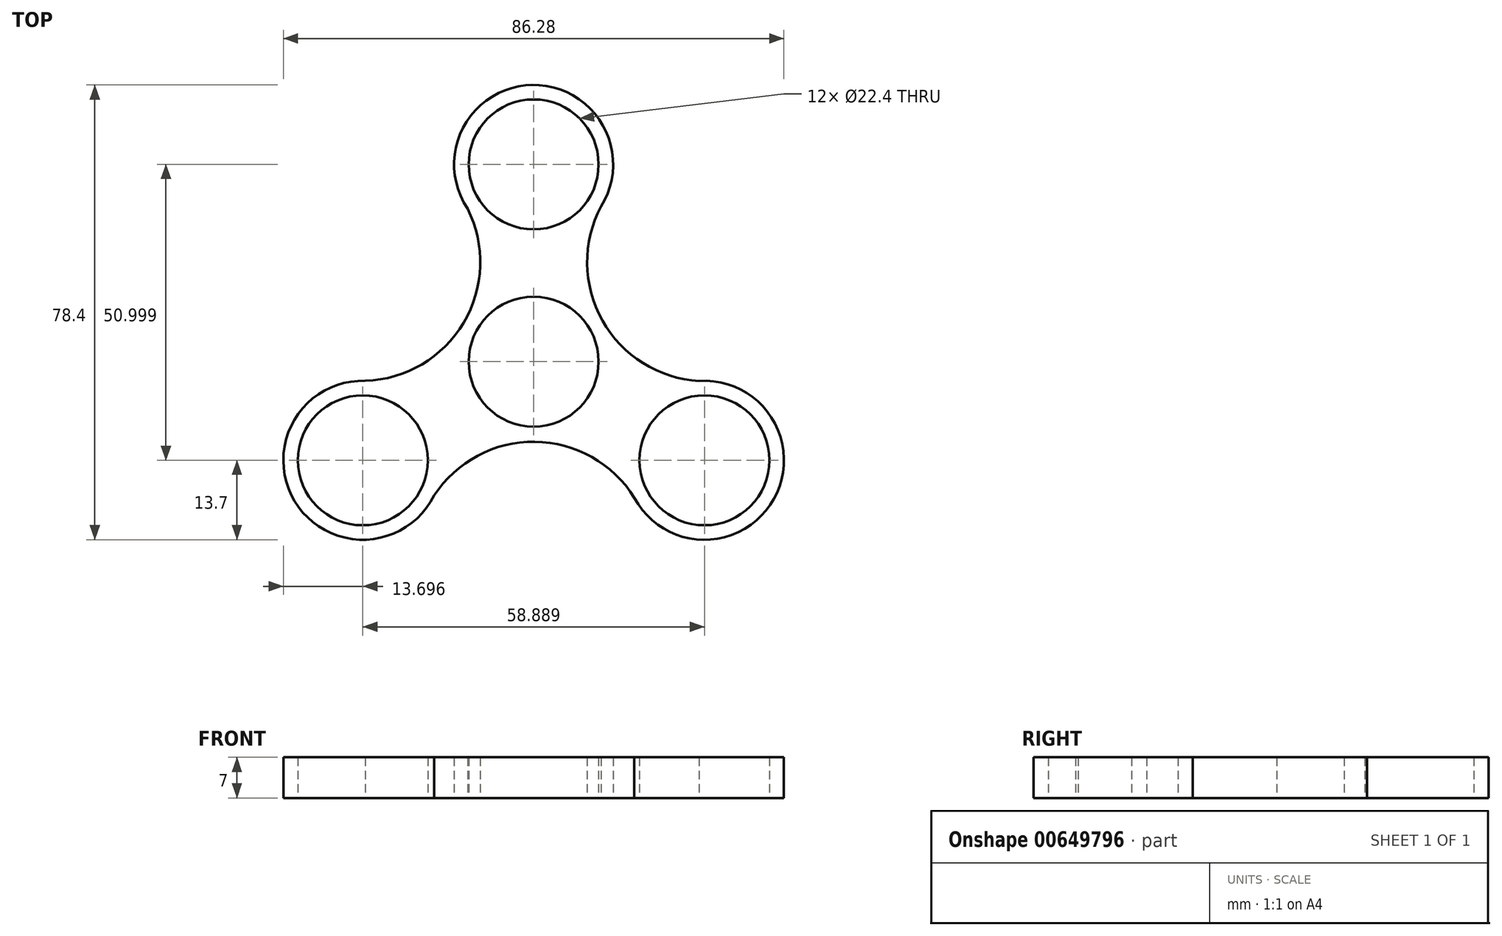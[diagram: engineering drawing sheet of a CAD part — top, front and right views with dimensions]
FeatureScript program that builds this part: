
annotation { "Feature Type Name" : "Feature", "Feature Type Description" : "" }
export const myFeature = defineFeature(function(context is Context, id is Id, definition is map)
    precondition{}
    {
        {
            var Q0;
            Q0=qCreatedBy(makeId("Top.planeOp"),FACE);
            var sketch = newSketch(context, id + "F0", { "sketchPlane" : qUnion([Q0])});
            skCircle(sketch, "E0", {"center": v(0, 0) * mm, "radius": 11.2 * mm});
            skCircle(sketch, "E1", {"center": v(0, 34) * mm, "radius": 11.2 * mm});
            skArc(sketch, "E2", {"start": v(11.63, 26.76) * mm, "mid": v(-0.23, 47.7) * mm, "end": v(-11.39, 26.38) * mm});
            skArc(sketch, "E3.1.0", {"start": v(-29, -3.3) * mm, "mid": v(-41.2, -24.05) * mm, "end": v(-17.15, -23.05) * mm});
            skCircle(sketch, "E3.1.1", {"center": v(-29.44, -17) * mm, "radius": 11.2 * mm});
            skArc(sketch, "E3.2.0", {"start": v(17.36, -23.45) * mm, "mid": v(41.42, -23.65) * mm, "end": v(28.54, -3.33) * mm});
            skCircle(sketch, "E3.2.1", {"center": v(29.44, -17) * mm, "radius": 11.2 * mm});
            skArc(sketch, "E4", {"start": v(-29, -3.3) * mm, "mid": v(-12.07, 6.72) * mm, "end": v(-11.39, 26.38) * mm});
            skArc(sketch, "E5.1.0", {"start": v(17.36, -23.45) * mm, "mid": v(0.21, -13.8) * mm, "end": v(-17.15, -23.05) * mm});
            skArc(sketch, "E5.2.0", {"start": v(11.63, 26.76) * mm, "mid": v(11.85, 7.09) * mm, "end": v(28.54, -3.33) * mm});
            skSolve(sketch);
        }
        {
            var Q0;
            Q0=makeQuery(id+"F0.imprint","IMPRINT",FACE,{"disambiguationData":[TD([[makeQuery(id+"F0.imprint","IMPRINT",EDGE,{"derivedFrom":sQuery(id+"F0.wireOp",EDGE,"E0")}),-1.0]])]});
            extrude(context, id + "F1", {"entities" : qUnion([Q0]), "depth" : 7 * mm, "offsetDistance" : 25 * mm});
        }
    });
